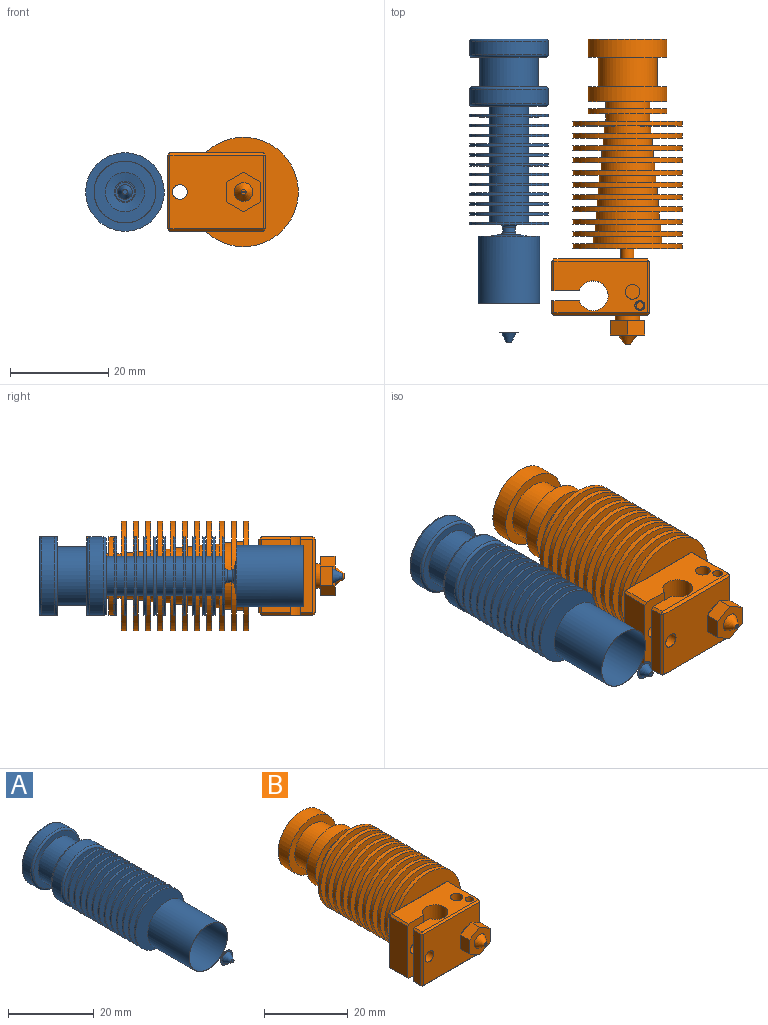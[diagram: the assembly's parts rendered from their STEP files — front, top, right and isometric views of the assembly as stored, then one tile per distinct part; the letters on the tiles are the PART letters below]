
ASSEMBLY  parts=2 mates=1
PART A: 72 faces, bbox 17.3x61.9x17.3 mm
  f0: cylinder r=8mm len=16mm, axis (0,-1,0), area 135.7mm2, adj f1,f38
  f1: torus R=7.5mm, axis (0,-1,0), area 38.6mm2, adj f0,f71
  f2: cylinder r=6mm len=12mm, axis (0,-1,0), area 226.2mm2, adj f70,f71
  f3: torus R=7.5mm, axis (0,-1,0), area 38.6mm2, adj f4,f70
  f4: cylinder r=8mm len=16mm, axis (0,-1,0), area 150.8mm2, adj f3,f5
  f5: torus R=7.5mm, axis (0,-1,0), area 38.6mm2, adj f4,f69
  f6: cylinder r=4mm len=8mm, axis (0,-1,0), area 41.5mm2, adj f68,f69
  f7: cylinder r=8mm len=16mm, axis (0,-1,0), area 25.1mm2, adj f67,f68
  f8: cylinder r=4mm len=8mm, axis (0,-1,0), area 37.7mm2, adj f66,f67
  f9: cylinder r=8mm len=16mm, axis (0,-1,0), area 25.1mm2, adj f65,f66
  f10: cylinder r=4mm len=8mm, axis (0,-1,0), area 37.7mm2, adj f64,f65
  f11: cylinder r=8mm len=16mm, axis (0,-1,0), area 25.1mm2, adj f63,f64
  f12: cylinder r=4mm len=8mm, axis (0,-1,0), area 37.7mm2, adj f62,f63
  f13: cylinder r=8mm len=16mm, axis (0,-1,0), area 25.1mm2, adj f61,f62
  f14: cylinder r=4mm len=8mm, axis (0,-1,0), area 37.7mm2, adj f60,f61
  f15: cylinder r=8mm len=16mm, axis (0,-1,0), area 25.1mm2, adj f59,f60
  f16: cylinder r=4mm len=8mm, axis (0,-1,0), area 37.7mm2, adj f58,f59
  f17: cylinder r=8mm len=16mm, axis (0,-1,0), area 25.1mm2, adj f57,f58
  f18: cylinder r=4mm len=8mm, axis (0,-1,0), area 37.7mm2, adj f56,f57
  f19: cylinder r=8mm len=16mm, axis (0,-1,0), area 25.1mm2, adj f55,f56
  f20: cylinder r=4mm len=8mm, axis (0,-1,0), area 37.7mm2, adj f54,f55
  f21: cylinder r=8mm len=16mm, axis (0,-1,0), area 25.1mm2, adj f53,f54
  f22: cylinder r=4mm len=8mm, axis (0,-1,0), area 37.7mm2, adj f52,f53
  f23: cylinder r=8mm len=16mm, axis (0,-1,0), area 25.1mm2, adj f51,f52
  f24: cylinder r=4mm len=8mm, axis (0,-1,0), area 37.7mm2, adj f50,f51
  f25: cylinder r=8mm len=16mm, axis (0,-1,0), area 25.1mm2, adj f49,f50
  f26: cylinder r=4mm len=8mm, axis (0,-1,0), area 37.7mm2, adj f48,f49
  f27: cylinder r=8mm len=16mm, axis (0,-1,0), area 25.1mm2, adj f47,f48
  f28: cylinder r=4mm len=8mm, axis (0,-1,0), area 37.7mm2, adj f46,f47
  f29: cylinder r=8mm len=16mm, axis (0,-1,0), area 25.1mm2, adj f45,f46
  f30: torus R=1.8mm, axis (0,-1,0), area 7.3mm2, adj f31,f45
  f31: cylinder r=1.3mm len=2.6mm, axis (0,-1,0), area 8.2mm2, adj f30,f32
  f32: torus R=1.8mm, axis (0,-1,0), area 7.3mm2, adj f31,f44
  f33: cone r=4mm half-angle=80deg, axis (0,-1,0), area 36.1mm2, adj f43,f44
  f34: cylinder r=6.3mm len=13.68mm, axis (0,-1,0), area 541.4mm2, adj f35,f43
  f35: sphere r=6.3mm, area 238.1mm2, adj f34,f42
  f36: cone r=0.5mm half-angle=26.6deg, axis (0,1,0), area 13.9mm2, adj f41,f42
  f37: cone r=2.2mm half-angle=45deg, axis (0,1,0), area 17.1mm2, adj f39,f40
  f38: torus R=7.5mm, axis (0,-1,0), area 38.6mm2, adj f0,f39
  f39: plane 15x15mm, normal (0,1,0), area 161.5mm2, adj f37,f38
  f40: plane 2x2mm, normal (0,1,0), area 3.1mm2, adj f37
  f41: plane 1x1mm, normal (0,-1,0), area 0.8mm2, adj f36
  f42: plane 3.9x3.9mm, normal (0,-1,0), area 4.9mm2, adj f35,f36
  f43: plane 12.6x12.6mm, normal (0,1,0), area 74.4mm2, adj f33,f34
  f44: plane 4.33x4.33mm, normal (0,1,0), area 4.5mm2, adj f32,f33
  f45: plane 16x16mm, normal (0,-1,0), area 190.9mm2, adj f29,f30
  f46: plane 16x16mm, normal (0,1,0), area 150.8mm2, adj f28,f29
  f47: plane 16x16mm, normal (0,-1,0), area 150.8mm2, adj f27,f28
  f48: plane 16x16mm, normal (0,1,0), area 150.8mm2, adj f26,f27
  f49: plane 16x16mm, normal (0,-1,0), area 150.8mm2, adj f25,f26
  f50: plane 16x16mm, normal (0,1,0), area 150.8mm2, adj f24,f25
  f51: plane 16x16mm, normal (0,-1,0), area 150.8mm2, adj f23,f24
  f52: plane 16x16mm, normal (0,1,0), area 150.8mm2, adj f22,f23
  f53: plane 16x16mm, normal (0,-1,0), area 150.8mm2, adj f21,f22
  f54: plane 16x16mm, normal (0,1,0), area 150.8mm2, adj f20,f21
  f55: plane 16x16mm, normal (0,-1,0), area 150.8mm2, adj f19,f20
  f56: plane 16x16mm, normal (0,1,0), area 150.8mm2, adj f18,f19
  f57: plane 16x16mm, normal (0,-1,0), area 150.8mm2, adj f17,f18
  f58: plane 16x16mm, normal (0,1,0), area 150.8mm2, adj f16,f17
  f59: plane 16x16mm, normal (0,-1,0), area 150.8mm2, adj f15,f16
  f60: plane 16x16mm, normal (0,1,0), area 150.8mm2, adj f14,f15
  f61: plane 16x16mm, normal (0,-1,0), area 150.8mm2, adj f13,f14
  f62: plane 16x16mm, normal (0,1,0), area 150.8mm2, adj f12,f13
  f63: plane 16x16mm, normal (0,-1,0), area 150.8mm2, adj f11,f12
  f64: plane 16x16mm, normal (0,1,0), area 150.8mm2, adj f10,f11
  f65: plane 16x16mm, normal (0,-1,0), area 150.8mm2, adj f9,f10
  f66: plane 16x16mm, normal (0,1,0), area 150.8mm2, adj f8,f9
  f67: plane 16x16mm, normal (0,-1,0), area 150.8mm2, adj f7,f8
  f68: plane 16x16mm, normal (0,1,0), area 150.8mm2, adj f6,f7
  f69: plane 15x15mm, normal (0,-1,0), area 126.4mm2, adj f5,f6
  f70: plane 15x15mm, normal (0,1,0), area 63.6mm2, adj f2,f3
  f71: plane 15x15mm, normal (0,-1,0), area 63.6mm2, adj f1,f2
PART B: 111 faces, bbox 26.7x62.3x22.3 mm
  f0: plane 0.5x0.5mm, normal (-0.58,0.58,-0.58), area 0.2mm2, adj f18,f20,f21
  f1: plane 0.5x0.5mm, normal (0.58,0.58,-0.58), area 0.2mm2, adj f4,f17,f20
  f2: plane 0.5x0.5mm, normal (-0.58,0.58,0.58), area 0.2mm2, adj f6,f18,f19
  f3: plane 0.5x0.5mm, normal (0.58,-0.58,-0.58), area 0.2mm2, adj f4,f9,f16
  f4: plane 10.5x0.5mm, normal (0.71,0,-0.71), area 7.4mm2, adj f1,f3,f27,f51
  f5: plane 0.5x0.5mm, normal (0.58,0.58,0.58), area 0.2mm2, adj f6,f11,f17
  f6: plane 19x0.5mm, normal (0,0.71,0.71), area 13.4mm2, adj f2,f5,f22,f25
  f7: plane 0.5x0.5mm, normal (-0.58,-0.58,-0.58), area 0.2mm2, adj f8,f9,f14
  f8: plane 2.5x0.5mm, normal (-0.71,0,-0.71), area 1.8mm2, adj f7,f50,f51,f52
  f9: plane 19x0.5mm, normal (0,-0.71,-0.71), area 13.4mm2, adj f3,f7,f26,f51
  f10: plane 0.5x0.5mm, normal (0.58,-0.58,0.58), area 0.2mm2, adj f11,f15,f16
  f11: plane 10.5x0.5mm, normal (0.71,0,0.71), area 7.4mm2, adj f5,f10,f22,f27
  f12: plane 0.5x0.5mm, normal (-0.58,-0.58,0.58), area 0.2mm2, adj f13,f14,f15
  f13: plane 2.5x0.5mm, normal (-0.71,0,0.71), area 1.8mm2, adj f12,f22,f50,f52
  f14: plane 15x0.5mm, normal (-0.71,-0.71,0), area 10.6mm2, adj f7,f12,f26,f52
  f15: plane 19x0.5mm, normal (0,-0.71,0.71), area 13.4mm2, adj f10,f12,f22,f26
  f16: plane 15x0.5mm, normal (0.71,-0.71,0), area 10.6mm2, adj f3,f10,f26,f27
  f17: plane 15x0.5mm, normal (0.71,0.71,0), area 10.6mm2, adj f1,f5,f25,f27
  f18: plane 15x0.5mm, normal (-0.71,0.71,0), area 10.6mm2, adj f0,f2,f23,f25
  f19: plane 6x0.5mm, normal (-0.71,0,0.71), area 4.2mm2, adj f2,f22,f23,f24
  f20: plane 19x0.5mm, normal (0,0.71,-0.71), area 13.4mm2, adj f0,f1,f25,f51
  f21: plane 6x0.5mm, normal (-0.71,0,-0.71), area 4.2mm2, adj f0,f23,f24,f51
  f22: plane 19x10.5mm, normal (0,0,1), area 150.5mm2, adj f6,f11,f13,f15,f19,f24,f43,f47
  f23: plane 15x6mm, normal (-1,0,0), area 90mm2, adj f18,f19,f21,f24
  f24: plane 16x5.65mm, normal (0,-1,0), area 83mm2, adj f19,f21,f22,f23,f42,f49,f51
  f25: plane 19x15mm, normal (0,1,0), area 271.8mm2, adj f6,f17,f18,f20,f42,f53
  f26: plane 19x15mm, normal (0,-1,0), area 258.3mm2, adj f9,f14,f15,f16,f40,f41
  f27: plane 15x10.5mm, normal (1,0,0), area 157.5mm2, adj f4,f11,f16,f17
  f28: cylinder r=0.2mm len=3mm, axis (0,1,0), area 3.8mm2, adj f29,f30
  f29: plane 0.4x0.4mm, normal (0,-1,0), area 0.1mm2, adj f28
  f30: plane 1x1mm, normal (0,-1,0), area 0.7mm2, adj f28,f31
  f31: cone r=1.9mm half-angle=35deg, axis (0,1,0), area 18.4mm2, adj f30,f39
  f32: plane 8.08x7mm, normal (0,1,0), area 22.8mm2, adj f33,f34,f35,f36,f37,f38,f40
  f33: plane 3.5x3mm, normal (-0.5,0,0.87), area 12.1mm2, adj f32,f34,f38,f39
  f34: plane 3.5x3mm, normal (0.5,0,0.87), area 12.1mm2, adj f32,f33,f35,f39
  f35: plane 4.04x3mm, normal (1,0,0), area 12.1mm2, adj f32,f34,f36,f39
  f36: plane 3.5x3mm, normal (0.5,0,-0.87), area 12.1mm2, adj f32,f35,f37,f39
  f37: plane 3.5x3mm, normal (-0.5,0,-0.87), area 12.1mm2, adj f32,f36,f38,f39
  f38: plane 4.04x3mm, normal (-1,0,0), area 12.1mm2, adj f32,f33,f37,f39
  f39: plane 8.08x7mm, normal (0,-1,0), area 31.1mm2, adj f31,f33,f34,f35,f36,f37,f38
  f40: cylinder r=2.5mm len=5mm, axis (0,-1,0), area 15.7mm2, adj f26,f32
  f41: cylinder r=1.5mm len=3mm, axis (0,-1,0), area 28.3mm2, adj f26,f50
  f42: cylinder r=1.5mm len=6.5mm, axis (0,-1,0), area 61.3mm2, adj f24,f25
  f43: cylinder r=1mm len=2mm, axis (0,0,-1), area 12.6mm2, adj f22,f44
  f44: plane 2x2mm, normal (0,0,1), area 1.3mm2, adj f43,f45
  f45: cylinder r=0.78mm len=2.45mm, axis (0,0,-1), area 11.9mm2, adj f44,f46
  f46: plane 1.55x1.55mm, normal (0,0,1), area 1.9mm2, adj f45
  f47: cylinder r=1.5mm len=3.45mm, axis (0,0,-1), area 32.5mm2, adj f22,f48
  f48: plane 3x3mm, normal (0,0,1), area 7.1mm2, adj f47
  f49: cylinder r=3.02mm len=16mm, axis (0,0,-1), area 271.5mm2, adj f22,f24,f50,f51
  f50: plane 16x5.65mm, normal (0,1,0), area 83mm2, adj f8,f13,f22,f41,f49,f51,f52
  f51: plane 19x10.5mm, normal (0,0,-1), area 160.7mm2, adj f4,f8,f9,f20,f21,f24,f49,f50
  f52: plane 15x2.5mm, normal (-1,0,0), area 37.5mm2, adj f8,f13,f14,f50
  f53: cylinder r=1.4mm len=2.8mm, axis (0,-1,0), area 18.5mm2, adj f25,f110
  f54: cylinder r=4mm len=8mm, axis (0,-1,0), area 163.4mm2, adj f55,f56
  f55: plane 8x8mm, normal (0,1,0), area 50.3mm2, adj f54
  f56: plane 16x16mm, normal (0,1,0), area 150.8mm2, adj f54,f57
  f57: cylinder r=8mm len=16mm, axis (0,-1,0), area 186mm2, adj f56,f58
  f58: plane 16x16mm, normal (0,-1,0), area 88mm2, adj f57,f59
  f59: cylinder r=6mm len=12mm, axis (0,-1,0), area 226.2mm2, adj f58,f60
  f60: plane 16x16mm, normal (0,1,0), area 88mm2, adj f59,f61
  f61: cylinder r=8mm len=16mm, axis (0,-1,0), area 150.8mm2, adj f60,f62
  f62: plane 16x16mm, normal (0,-1,0), area 137.4mm2, adj f61,f63
  f63: cylinder r=4.5mm len=9mm, axis (0,-1,0), area 42.4mm2, adj f62,f64
  f64: plane 16x16mm, normal (0,1,0), area 137.4mm2, adj f63,f65
  f65: cylinder r=8mm len=16mm, axis (0,-1,0), area 50.3mm2, adj f64,f66
  f66: plane 16x16mm, normal (0,-1,0), area 137.4mm2, adj f65,f67
  f67: cylinder r=4.5mm len=9mm, axis (0,-1,0), area 42.4mm2, adj f66,f68
  f68: plane 22.3x22.3mm, normal (0,1,0), area 327mm2, adj f67,f69
  f69: cylinder r=11.15mm len=22.3mm, axis (0,-1,0), area 70.1mm2, adj f68,f70
  f70: plane 22.3x22.3mm, normal (0,-1,0), area 319.7mm2, adj f69,f71
  f71: cylinder r=4.75mm len=9.5mm, axis (0,-1,0), area 44.8mm2, adj f70,f72
  f72: plane 22.3x22.3mm, normal (0,1,0), area 319.7mm2, adj f71,f73
  f73: cylinder r=11.15mm len=22.3mm, axis (0,-1,0), area 70.1mm2, adj f72,f74
  f74: plane 22.3x22.3mm, normal (0,-1,0), area 312mm2, adj f73,f75
  f75: cylinder r=5mm len=10mm, axis (0,-1,0), area 47.1mm2, adj f74,f76
  f76: plane 22.3x22.3mm, normal (0,1,0), area 312mm2, adj f75,f77
  f77: cylinder r=11.15mm len=22.3mm, axis (0,-1,0), area 70.1mm2, adj f76,f78
  f78: plane 22.3x22.3mm, normal (0,-1,0), area 304mm2, adj f77,f79
  f79: cylinder r=5.25mm len=10.5mm, axis (0,-1,0), area 49.5mm2, adj f78,f80
  f80: plane 22.3x22.3mm, normal (0,1,0), area 304mm2, adj f79,f81
  f81: cylinder r=11.15mm len=22.3mm, axis (0,-1,0), area 70.1mm2, adj f80,f82
  f82: plane 22.3x22.3mm, normal (0,-1,0), area 295.5mm2, adj f81,f83
  f83: cylinder r=5.5mm len=11mm, axis (0,-1,0), area 51.8mm2, adj f82,f84
  f84: plane 22.3x22.3mm, normal (0,1,0), area 295.5mm2, adj f83,f85
  f85: cylinder r=11.15mm len=22.3mm, axis (0,-1,0), area 70.1mm2, adj f84,f86
  f86: plane 22.3x22.3mm, normal (0,-1,0), area 286.7mm2, adj f85,f87
  f87: cylinder r=5.75mm len=11.5mm, axis (0,-1,0), area 54.2mm2, adj f86,f88
  f88: plane 22.3x22.3mm, normal (0,1,0), area 286.7mm2, adj f87,f89
  f89: cylinder r=11.15mm len=22.3mm, axis (0,-1,0), area 70.1mm2, adj f88,f90
  f90: plane 22.3x22.3mm, normal (0,-1,0), area 277.5mm2, adj f89,f91
  f91: cylinder r=6mm len=12mm, axis (0,-1,0), area 56.5mm2, adj f90,f92
  f92: plane 22.3x22.3mm, normal (0,1,0), area 277.5mm2, adj f91,f93
  f93: cylinder r=11.15mm len=22.3mm, axis (0,-1,0), area 70.1mm2, adj f92,f94
  f94: plane 22.3x22.3mm, normal (0,-1,0), area 267.9mm2, adj f93,f95
  f95: cylinder r=6.25mm len=12.5mm, axis (0,-1,0), area 58.9mm2, adj f94,f96
  f96: plane 22.3x22.3mm, normal (0,1,0), area 267.9mm2, adj f95,f97
  f97: cylinder r=11.15mm len=22.3mm, axis (0,-1,0), area 70.1mm2, adj f96,f98
  f98: plane 22.3x22.3mm, normal (0,-1,0), area 257.8mm2, adj f97,f99
  f99: cylinder r=6.5mm len=13mm, axis (0,-1,0), area 61.3mm2, adj f98,f100
  f100: plane 22.3x22.3mm, normal (0,1,0), area 257.8mm2, adj f99,f101
  f101: cylinder r=11.15mm len=22.3mm, axis (0,-1,0), area 70.1mm2, adj f100,f102
  f102: plane 22.3x22.3mm, normal (0,-1,0), area 247.4mm2, adj f101,f103
  f103: cylinder r=6.75mm len=13.5mm, axis (0,-1,0), area 63.6mm2, adj f102,f104
  f104: plane 22.3x22.3mm, normal (0,1,0), area 247.4mm2, adj f103,f105
  f105: cylinder r=11.15mm len=22.3mm, axis (0,-1,0), area 70.1mm2, adj f104,f106
  f106: plane 22.3x22.3mm, normal (0,-1,0), area 236.6mm2, adj f105,f107
  f107: cylinder r=7mm len=14mm, axis (0,-1,0), area 66mm2, adj f106,f108
  f108: plane 22.3x22.3mm, normal (0,1,0), area 236.6mm2, adj f107,f109
  f109: cylinder r=11.15mm len=22.3mm, axis (0,-1,0), area 70.1mm2, adj f108,f110
  f110: plane 22.3x22.3mm, normal (0,-1,0), area 384.4mm2, adj f53,f109
PLACE A rot(axis=(0,1,0),90deg) t=(7.55,18.04,-48.8)mm
PLACE B t=(31.73,-0.28,-0.39)mm
MATE planar A.f36 <-> B.f53  axis (0,-1,0) through (7.55,17.37,-0.39)mm
